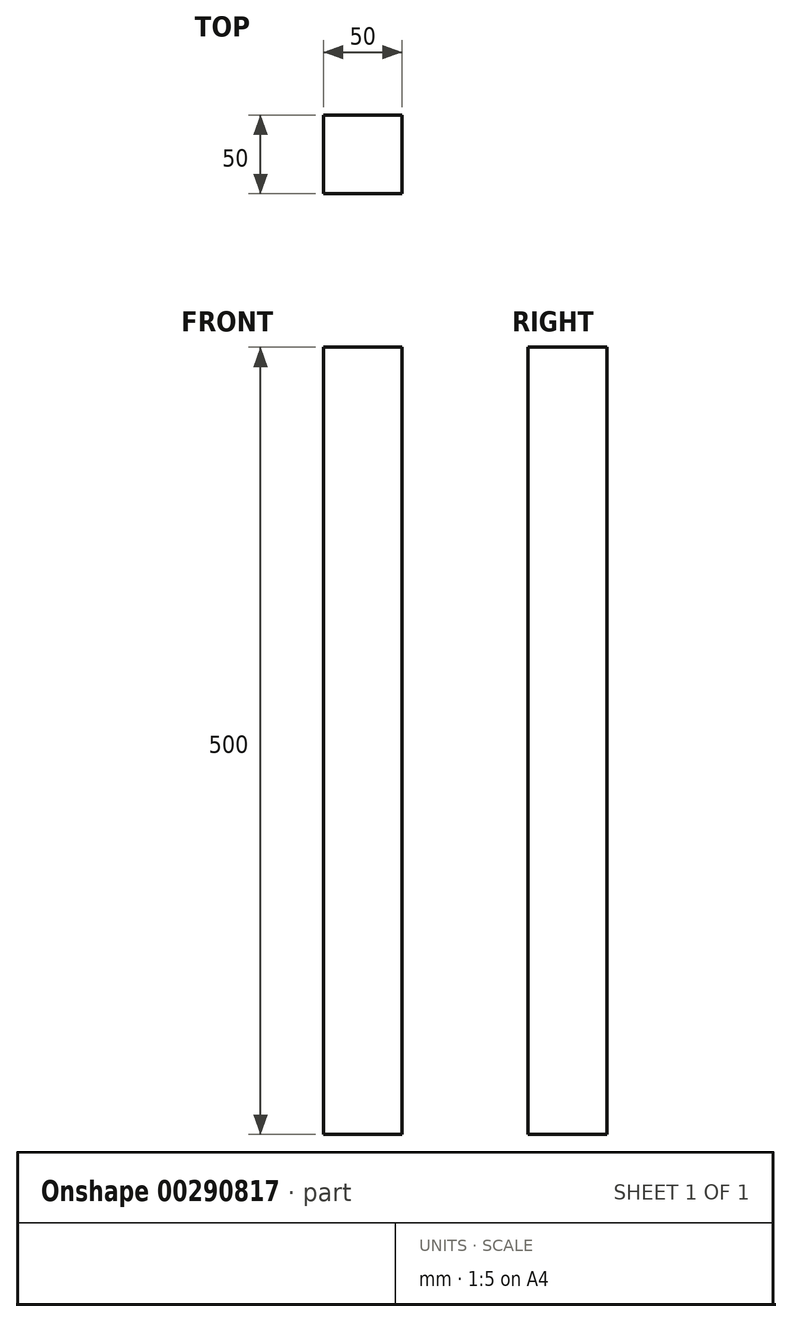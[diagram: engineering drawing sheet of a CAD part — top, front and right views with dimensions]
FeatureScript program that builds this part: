
annotation { "Feature Type Name" : "Feature", "Feature Type Description" : "" }
export const myFeature = defineFeature(function(context is Context, id is Id, definition is map)
    precondition{}
    {
        {
            var Q0;
            Q0=qCreatedBy(makeId("Top.planeOp"),FACE);
            var sketch = newSketch(context, id + "F0", { "sketchPlane" : qUnion([Q0])});
            skLineSegment(sketch, "E0.bottom", {"start": v(25, 25) * mm, "end": v(-25, 25) * mm});
            skLineSegment(sketch, "E0.top", {"start": v(25, -25) * mm, "end": v(-25, -25) * mm});
            skLineSegment(sketch, "E0.left", {"start": v(25, 25) * mm, "end": v(25, -25) * mm});
            skLineSegment(sketch, "E0.right", {"start": v(-25, 25) * mm, "end": v(-25, -25) * mm});
            skPoint(sketch, "E0.middle", {"position": v(0, 0) * mm});
            skSolve(sketch);
        }
        {
            var Q0;
            Q0=makeQuery(id+"F0.imprint","IMPRINT",FACE,{"disambiguationData":[TD([[makeQuery(id+"F0.imprint","IMPRINT",EDGE,{"derivedFrom":sQuery(id+"F0.wireOp",EDGE,"E0.bottom")}),1.0]])]});
            extrude(context, id + "F1", {"entities" : qUnion([Q0]), "depth" : 500 * mm});
        }
    });
